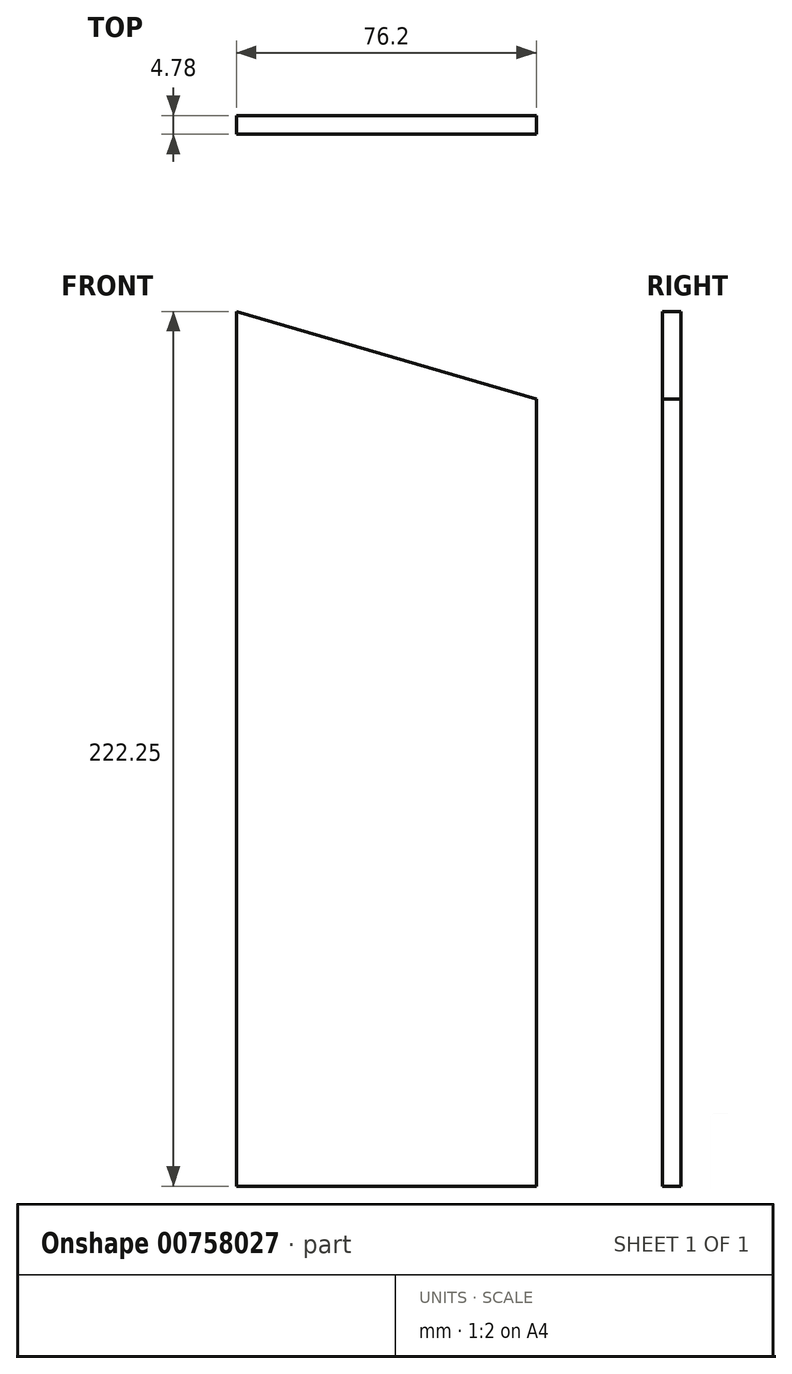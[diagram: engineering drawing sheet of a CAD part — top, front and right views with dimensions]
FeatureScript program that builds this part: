
annotation { "Feature Type Name" : "Feature", "Feature Type Description" : "" }
export const myFeature = defineFeature(function(context is Context, id is Id, definition is map)
    precondition{}
    {
        {
            var Q0;
            Q0=qCreatedBy(makeId("Front.planeOp"),FACE);
            var sketch = newSketch(context, id + "F0", { "sketchPlane" : qUnion([Q0])});
            skLineSegment(sketch, "E0", {"start": v(0, 0) * mm, "end": v(76.2, 0) * mm});
            skLineSegment(sketch, "E1", {"start": v(76.2, 0) * mm, "end": v(76.2, 200.03) * mm});
            skLineSegment(sketch, "E2", {"start": v(0, 0) * mm, "end": v(0, 222.25) * mm});
            skLineSegment(sketch, "E3", {"start": v(0, 222.25) * mm, "end": v(76.2, 200.03) * mm});
            skSolve(sketch);
        }
        {
            var Q0;
            Q0=makeQuery(id+"F0.imprint","IMPRINT",FACE,{"disambiguationData":[TD([[makeQuery(id+"F0.imprint","IMPRINT",EDGE,{"derivedFrom":sQuery(id+"F0.wireOp",EDGE,"E0")}),1.0]])]});
            extrude(context, id + "F1", {"entities" : qUnion([Q0]), "depth" : 4.78 * mm, "offsetDistance" : 25.4 * mm});
        }
    });
